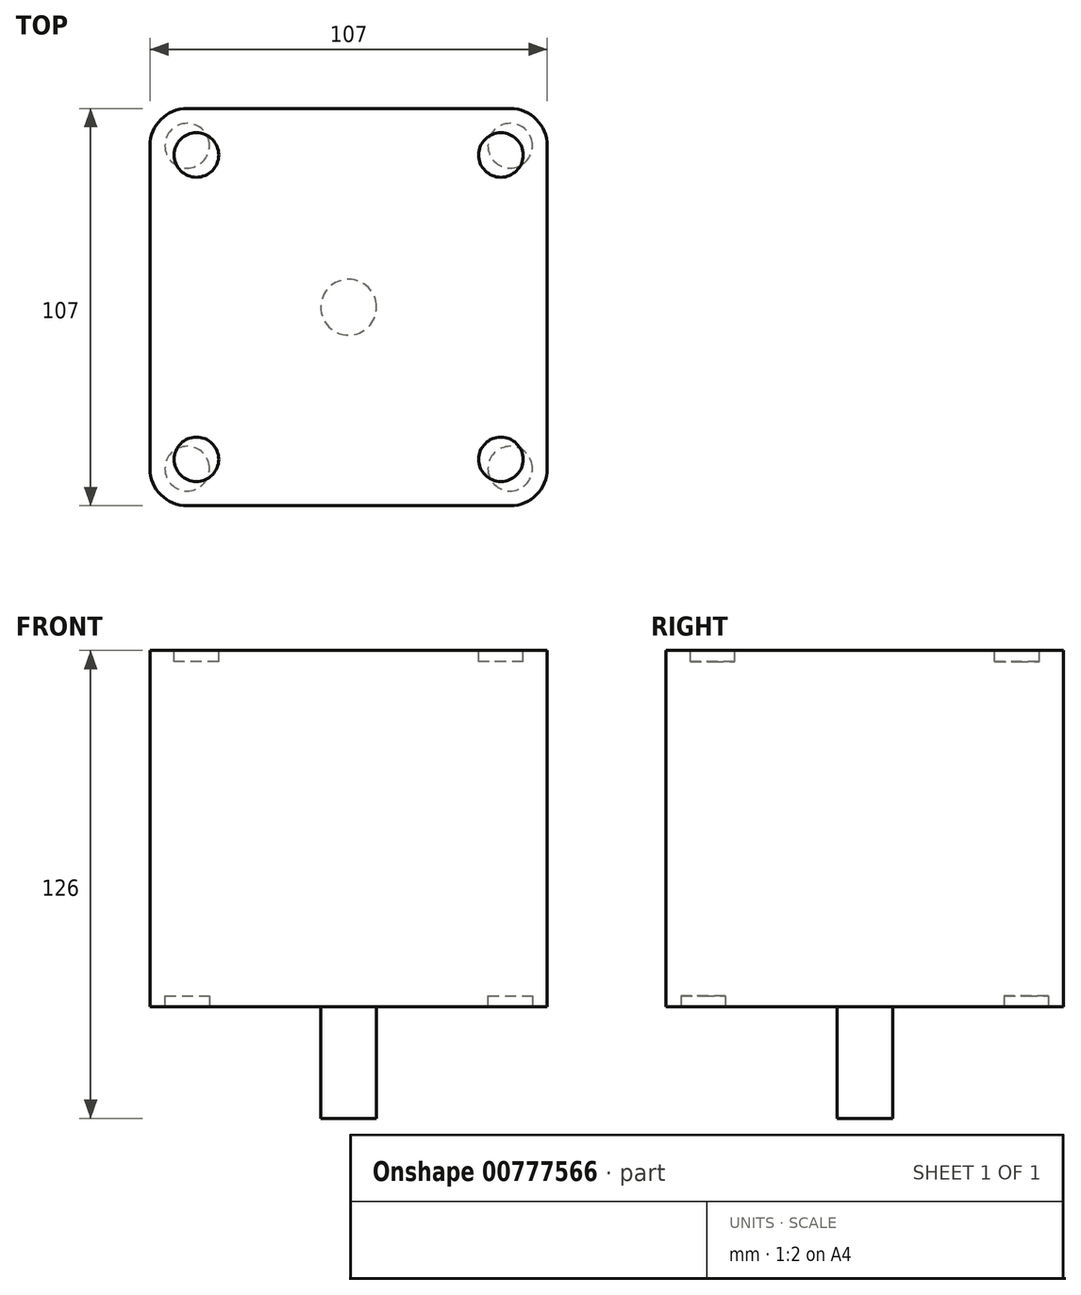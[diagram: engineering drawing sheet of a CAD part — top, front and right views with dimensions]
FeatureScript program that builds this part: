
annotation { "Feature Type Name" : "Feature", "Feature Type Description" : "" }
export const myFeature = defineFeature(function(context is Context, id is Id, definition is map)
    precondition{}
    {
        {
            var Q0;
            Q0=qCreatedBy(makeId("Top.planeOp"),FACE);
            var sketch = newSketch(context, id + "F0", { "sketchPlane" : qUnion([Q0])});
            skLineSegment(sketch, "E0.bottom", {"start": v(-10, 0) * mm, "end": v(-97, 0) * mm});
            skLineSegment(sketch, "E0.top", {"start": v(-10, -107) * mm, "end": v(-97, -107) * mm});
            skLineSegment(sketch, "E0.left", {"start": v(0, -10) * mm, "end": v(0, -97) * mm});
            skLineSegment(sketch, "E0.right", {"start": v(-107, -10) * mm, "end": v(-107, -97) * mm});
            skPoint(sketch, "E1.visualSharp", {"position": v(-107, 0) * mm});
            skArc(sketch, "E1.filletArc", {"start": v(-97, 0) * mm, "mid": v(-104.07, -2.93) * mm, "end": v(-107, -10) * mm});
            skPoint(sketch, "E2.visualSharp", {"position": v(-107, -107) * mm});
            skArc(sketch, "E2.filletArc", {"start": v(-107, -97) * mm, "mid": v(-104.07, -104.07) * mm, "end": v(-97, -107) * mm});
            skPoint(sketch, "E3.visualSharp", {"position": v(0, -107) * mm});
            skArc(sketch, "E3.filletArc", {"start": v(-10, -107) * mm, "mid": v(-2.93, -104.07) * mm, "end": v(0, -97) * mm});
            skPoint(sketch, "E4.visualSharp", {"position": v(0, 0) * mm});
            skArc(sketch, "E4.filletArc", {"start": v(0, -10) * mm, "mid": v(-2.93, -2.93) * mm, "end": v(-10, 0) * mm});
            skSolve(sketch);
        }
        {
            var Q0;
            Q0 = qSketchRegion(id + "F0", true);
            extrude(context, id + "F1", {"entities" : qUnion([Q0]), "depth" : 96 * mm, "offsetDistance" : 25 * mm});
        }
        {
            var Q0;
            Q0=makeQuery(id+"F1.opExtrude","CAP_FACE",FACE,{"disambiguationData":[OSD([sQuery(id+"F0.wireOp",EDGE,"E0.bottom"),sQuery(id+"F0.wireOp",EDGE,"E0.top"),sQuery(id+"F0.wireOp",EDGE,"E0.left"),sQuery(id+"F0.wireOp",EDGE,"E0.right"),sQuery(id+"F0.wireOp",EDGE,"E1.filletArc"),sQuery(id+"F0.wireOp",EDGE,"E2.filletArc"),sQuery(id+"F0.wireOp",EDGE,"E3.filletArc"),sQuery(id+"F0.wireOp",EDGE,"E4.filletArc")])],"isStart":true});
            var sketch = newSketch(context, id + "F2", { "sketchPlane" : qUnion([Q0])});
            skCircle(sketch, "E5", {"center": v(-53.5, 53.5) * mm, "radius": 7.5 * mm});
            skPoint(sketch, "E5.centerSnap0", {"position": v(-107, 53.5) * mm});
            skPoint(sketch, "E5.centerSnap1", {"position": v(-53.5, 107) * mm});
            skSolve(sketch);
        }
        {
            var Q0;
            Q0 = qSketchRegion(id + "F2", true);
            extrude(context, id + "F3", {"entities" : qUnion([Q0]), "operationType" : NewBodyOperationType.ADD, "depth" : 30 * mm, "offsetDistance" : 25 * mm});
        }
        {
            var Q0;
            Q0=makeQuery(id+"F1.opExtrude","CAP_FACE",FACE,{"disambiguationData":[OSD([sQuery(id+"F0.wireOp",EDGE,"E0.bottom"),sQuery(id+"F0.wireOp",EDGE,"E0.top"),sQuery(id+"F0.wireOp",EDGE,"E0.left"),sQuery(id+"F0.wireOp",EDGE,"E0.right"),sQuery(id+"F0.wireOp",EDGE,"E1.filletArc"),sQuery(id+"F0.wireOp",EDGE,"E2.filletArc"),sQuery(id+"F0.wireOp",EDGE,"E3.filletArc"),sQuery(id+"F0.wireOp",EDGE,"E4.filletArc")])],"isStart":false});
            var sketch = newSketch(context, id + "F4", { "sketchPlane" : qUnion([Q0])});
            skCircle(sketch, "E6", {"center": v(-94.5, -94.5) * mm, "radius": 6 * mm});
            skCircle(sketch, "E7", {"center": v(-94.5, -12.5) * mm, "radius": 6 * mm});
            skCircle(sketch, "E8", {"center": v(-12.5, -94.5) * mm, "radius": 6 * mm});
            skCircle(sketch, "E9", {"center": v(-12.5, -12.5) * mm, "radius": 6 * mm});
            skLineSegment(sketch, "E10", {"start": v(-94.5, -94.5) * mm, "end": v(-12.5, -94.5) * mm, "construction": true});
            skPoint(sketch, "E11", {"position": v(-53.5, -94.5) * mm});
            skPoint(sketch, "E12", {"position": v(-53.5, -107) * mm});
            skPoint(sketch, "E13", {"position": v(-107, -53.5) * mm});
            skLineSegment(sketch, "E14", {"start": v(-94.5, -12.5) * mm, "end": v(-94.5, -94.5) * mm, "construction": true});
            skPoint(sketch, "E15", {"position": v(-94.5, -53.5) * mm});
            skSolve(sketch);
        }
        {
            var Q0;
            Q0 = qSketchRegion(id + "F4", true);
            extrude(context, id + "F5", {"entities" : qUnion([Q0]), "operationType" : NewBodyOperationType.REMOVE, "oppositeDirection" : true, "depth" : 3 * mm, "offsetDistance" : 25 * mm});
        }
        {
            var Q0;
            Q0=makeQuery(id+"F1.opExtrude","CAP_FACE",FACE,{"disambiguationData":[OSD([sQuery(id+"F0.wireOp",EDGE,"E0.bottom"),sQuery(id+"F0.wireOp",EDGE,"E0.top"),sQuery(id+"F0.wireOp",EDGE,"E0.left"),sQuery(id+"F0.wireOp",EDGE,"E0.right"),sQuery(id+"F0.wireOp",EDGE,"E1.filletArc"),sQuery(id+"F0.wireOp",EDGE,"E2.filletArc"),sQuery(id+"F0.wireOp",EDGE,"E3.filletArc"),sQuery(id+"F0.wireOp",EDGE,"E4.filletArc")])],"isStart":true});
            var sketch = newSketch(context, id + "F6", { "sketchPlane" : qUnion([Q0])});
            skCircle(sketch, "E16", {"center": v(-10, 97) * mm, "radius": 6 * mm});
            skCircle(sketch, "E17", {"center": v(-10, 10) * mm, "radius": 6 * mm});
            skCircle(sketch, "E18", {"center": v(-97, 97) * mm, "radius": 6 * mm});
            skCircle(sketch, "E19", {"center": v(-97, 10) * mm, "radius": 6 * mm});
            skSolve(sketch);
        }
        {
            var Q0;
            Q0 = qSketchRegion(id + "F6", true);
            extrude(context, id + "F7", {"entities" : qUnion([Q0]), "operationType" : NewBodyOperationType.REMOVE, "oppositeDirection" : true, "depth" : 3 * mm, "offsetDistance" : 25 * mm});
        }
    });
